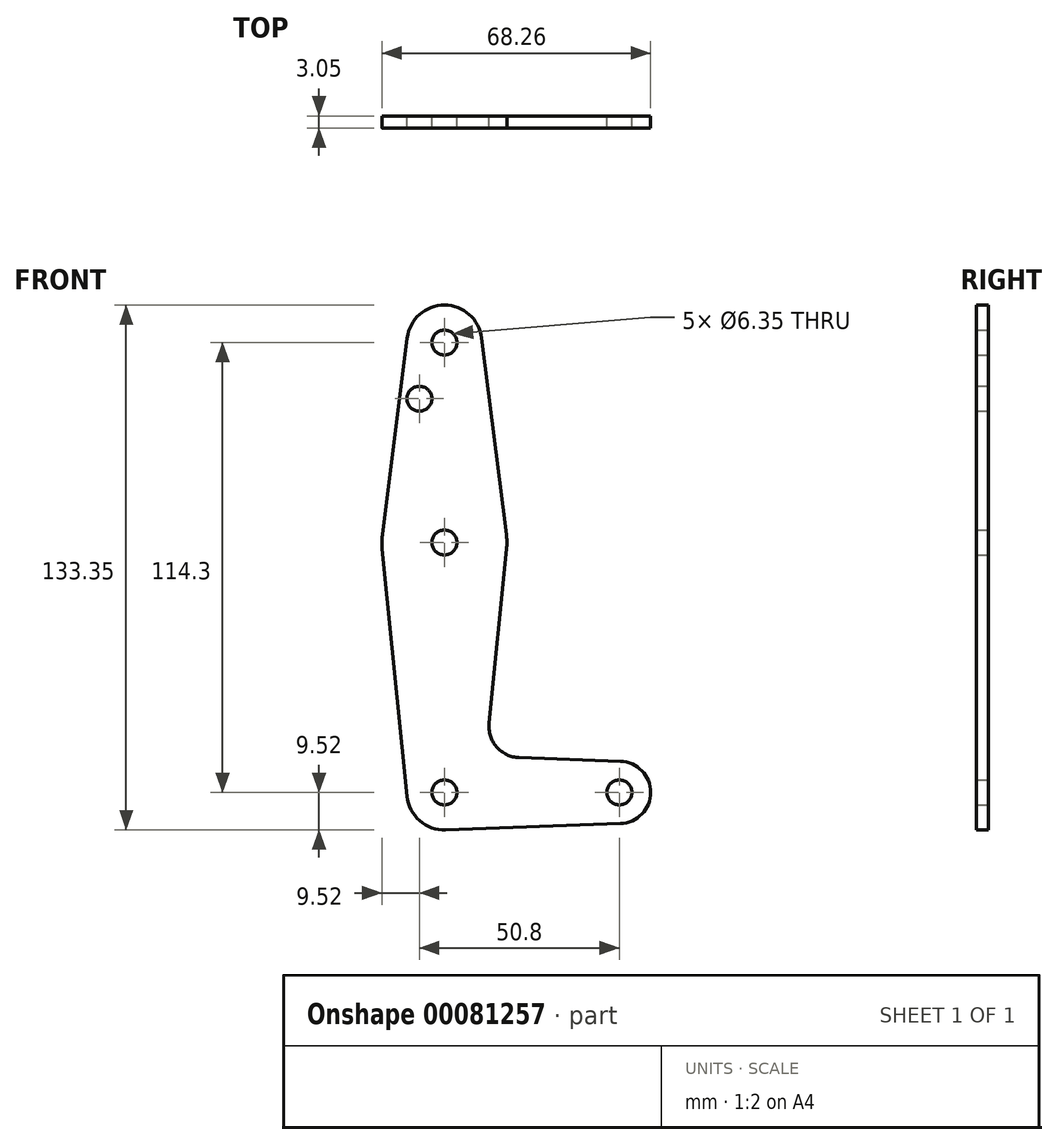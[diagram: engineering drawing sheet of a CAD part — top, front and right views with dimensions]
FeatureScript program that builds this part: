
annotation { "Feature Type Name" : "Feature", "Feature Type Description" : "" }
export const myFeature = defineFeature(function(context is Context, id is Id, definition is map)
    precondition{}
    {
        {
            var Q0;
            Q0=qCreatedBy(makeId("Front.planeOp"),FACE);
            var sketch = newSketch(context, id + "F0", { "sketchPlane" : qUnion([Q0])});
            skCircle(sketch, "E0", {"center": v(0, 0) * mm, "radius": 9.53 * mm});
            skCircle(sketch, "E1", {"center": v(44.45, 0) * mm, "radius": 7.94 * mm});
            skCircle(sketch, "E2", {"center": v(0, 63.5) * mm, "radius": 15.88 * mm});
            skCircle(sketch, "E3", {"center": v(0, 114.3) * mm, "radius": 9.53 * mm});
            skLineSegment(sketch, "E4", {"start": v(0, 114.3) * mm, "end": v(0, 0) * mm, "construction": true});
            skLineSegment(sketch, "E5", {"start": v(0, 0) * mm, "end": v(44.45, 0) * mm, "construction": true});
            skLineSegment(sketch, "E6", {"start": v(-9.48, -0.95) * mm, "end": v(-15.8, 61.91) * mm});
            skLineSegment(sketch, "E7", {"start": v(11.34, 17.6) * mm, "end": v(15.8, 61.91) * mm});
            skLineSegment(sketch, "E8", {"start": v(15.75, 65.48) * mm, "end": v(9.45, 115.5) * mm});
            skLineSegment(sketch, "E9", {"start": v(-15.75, 65.48) * mm, "end": v(-9.45, 115.5) * mm});
            skLineSegment(sketch, "E10", {"start": v(0.34, -9.52) * mm, "end": v(44.73, -7.93) * mm});
            skLineSegment(sketch, "E11", {"start": v(18.97, 8.85) * mm, "end": v(44.73, 7.93) * mm});
            skCircle(sketch, "E12", {"center": v(0, 114.3) * mm, "radius": 3.18 * mm});
            skCircle(sketch, "E13", {"center": v(0, 63.5) * mm, "radius": 3.18 * mm});
            skCircle(sketch, "E14", {"center": v(0, 0) * mm, "radius": 3.18 * mm});
            skCircle(sketch, "E15", {"center": v(44.45, 0) * mm, "radius": 3.18 * mm});
            skCircle(sketch, "E16", {"center": v(-6.35, 100.03) * mm, "radius": 3.18 * mm});
            skArc(sketch, "E17.filletArc", {"start": v(11.34, 17.6) * mm, "mid": v(13.26, 11.57) * mm, "end": v(18.97, 8.85) * mm});
            skSolve(sketch);
        }
        {
            var Q0;
            Q0 = qSketchRegion(id + "F0", true);
            extrude(context, id + "F1", {"entities" : qUnion([Q0]), "depth" : 3.05 * mm});
        }
    });
